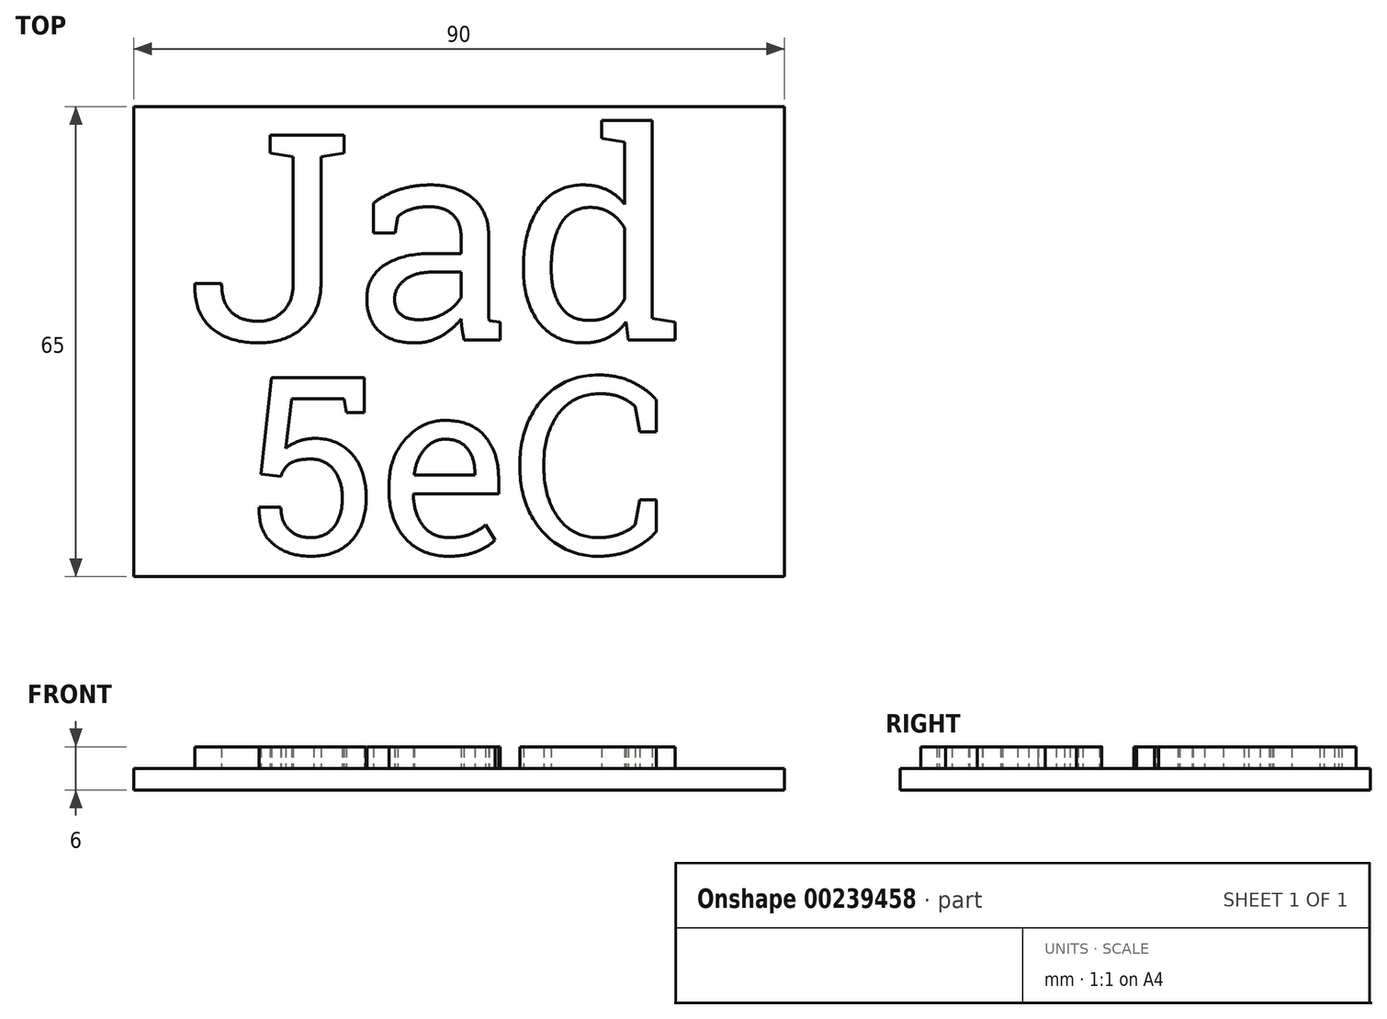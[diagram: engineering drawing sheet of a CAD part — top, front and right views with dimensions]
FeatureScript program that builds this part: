
annotation { "Feature Type Name" : "Feature", "Feature Type Description" : "" }
export const myFeature = defineFeature(function(context is Context, id is Id, definition is map)
    precondition{}
    {
        {
            var Q0;
            Q0=qCreatedBy(makeId("Top.planeOp"),FACE);
            var sketch = newSketch(context, id + "F0", { "sketchPlane" : qUnion([Q0])});
            skLineSegment(sketch, "E0.bottom", {"start": v(0, 0) * mm, "end": v(90, 0) * mm});
            skLineSegment(sketch, "E0.top", {"start": v(0, -65) * mm, "end": v(90, -65) * mm});
            skLineSegment(sketch, "E0.left", {"start": v(0, 0) * mm, "end": v(0, -65) * mm});
            skLineSegment(sketch, "E0.right", {"start": v(90, 0) * mm, "end": v(90, -65) * mm});
            skSolve(sketch);
        }
        {
            var Q0;
            Q0=makeQuery(id+"F0.imprint","IMPRINT",FACE,{"disambiguationData":[TD([[makeQuery(id+"F0.imprint","IMPRINT",EDGE,{"derivedFrom":sQuery(id+"F0.wireOp",EDGE,"E0.bottom")}),-1.0]])]});
            extrude(context, id + "F1", {"entities" : qUnion([Q0]), "depth" : 3 * mm});
        }
        {
            var Q0;
            Q0=makeQuery(id+"F1.opExtrude","CAP_FACE",FACE,{"disambiguationData":[OSD([sQuery(id+"F0.wireOp",EDGE,"E0.bottom"),sQuery(id+"F0.wireOp",EDGE,"E0.top"),sQuery(id+"F0.wireOp",EDGE,"E0.left"),sQuery(id+"F0.wireOp",EDGE,"E0.right")])],"isStart":false});
            var sketch = newSketch(context, id + "F2", { "sketchPlane" : qUnion([Q0])});
            skSolve(sketch);
        }
        {
            var Q0;
            Q0=makeQuery(id+"F2.imprint","IMPRINT",FACE,{"disambiguationData":[TD([[makeQuery(id+"F2.imprint","IMPRINT",EDGE,{"derivedFrom":makeQuery(id+"F1.opExtrude","CAP_EDGE",EDGE,{"disambiguationData":[OSD([sQuery(id+"F0.wireOp",EDGE,"E0.bottom")])],"isStart":false})}),-1.0]])]});
            var sketch = newSketch(context, id + "F3", { "sketchPlane" : qUnion([Q0])});
            skText(sketch, "E1", { "text": "Jad", "fontName": "RobotoSlab-Regular.ttf"});
            skText(sketch, "E2", { "text": " 5eC\n", "fontName": "RobotoSlab-Regular.ttf"});
            const initialGuessF3  = {"E1": [0.00721, -0.03227, 1, 0, 0.02869], "E2": [0.00721, -0.06182, 1, 0, 0.02467]};
            skSetInitialGuess(sketch, initialGuessF3);
            skSolve(sketch);
        }
        {
            var Q0;
            Q0 = qSketchRegion(id + "F3", true);
            extrude(context, id + "F4", {"entities" : qUnion([Q0]), "operationType" : NewBodyOperationType.ADD, "depth" : 2 * mm});
        }
        {
            var Q0;
            Q0 = qSketchRegion(id + "F3", true);
            extrude(context, id + "F5", {"entities" : qUnion([Q0]), "operationType" : NewBodyOperationType.ADD, "depth" : 3 * mm});
        }
    });
